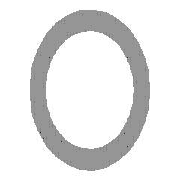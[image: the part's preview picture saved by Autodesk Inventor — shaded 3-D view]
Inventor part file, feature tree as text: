
AUTODESK INVENTOR PART (.ipt)
format: ipt  version: 2021 (Build 250183000, 183)  size: 120,832 bytes
history: native  units: mm (DEFAULTED — no unit token found)
features: other x5, plane x2, sketch x2, sweep x1
ambient origin geometry x8: Origin, YZ Plane, XZ Plane, XY Plane, X Axis, Y Axis, Z Axis, Center Point
bodies: Solid1 (feature_tree)
feature tree (10):
  parser-record x1  (decoder bookkeeping rows leaked as tree rows — omitted from the tree; the rows remain in map.json)
  other  "Driven Length"
  other  "Plano inicial"
  other  "Plano final"
  other  "Trayectoria de barrido"
  plane  "Plano de trabajo de orientación"
  sweep  "Cuerpo"
  sketch  "Sketch3"  dims[d0=60.452mm d1=5.5372mm]
  plane  "Work Plane3"
  sketch  "Sketch4"  dims[d4=-0.0mm d5=64.0mm d6=90.0deg d7=64.0mm d8=0.0mm d9=0.0mm]
